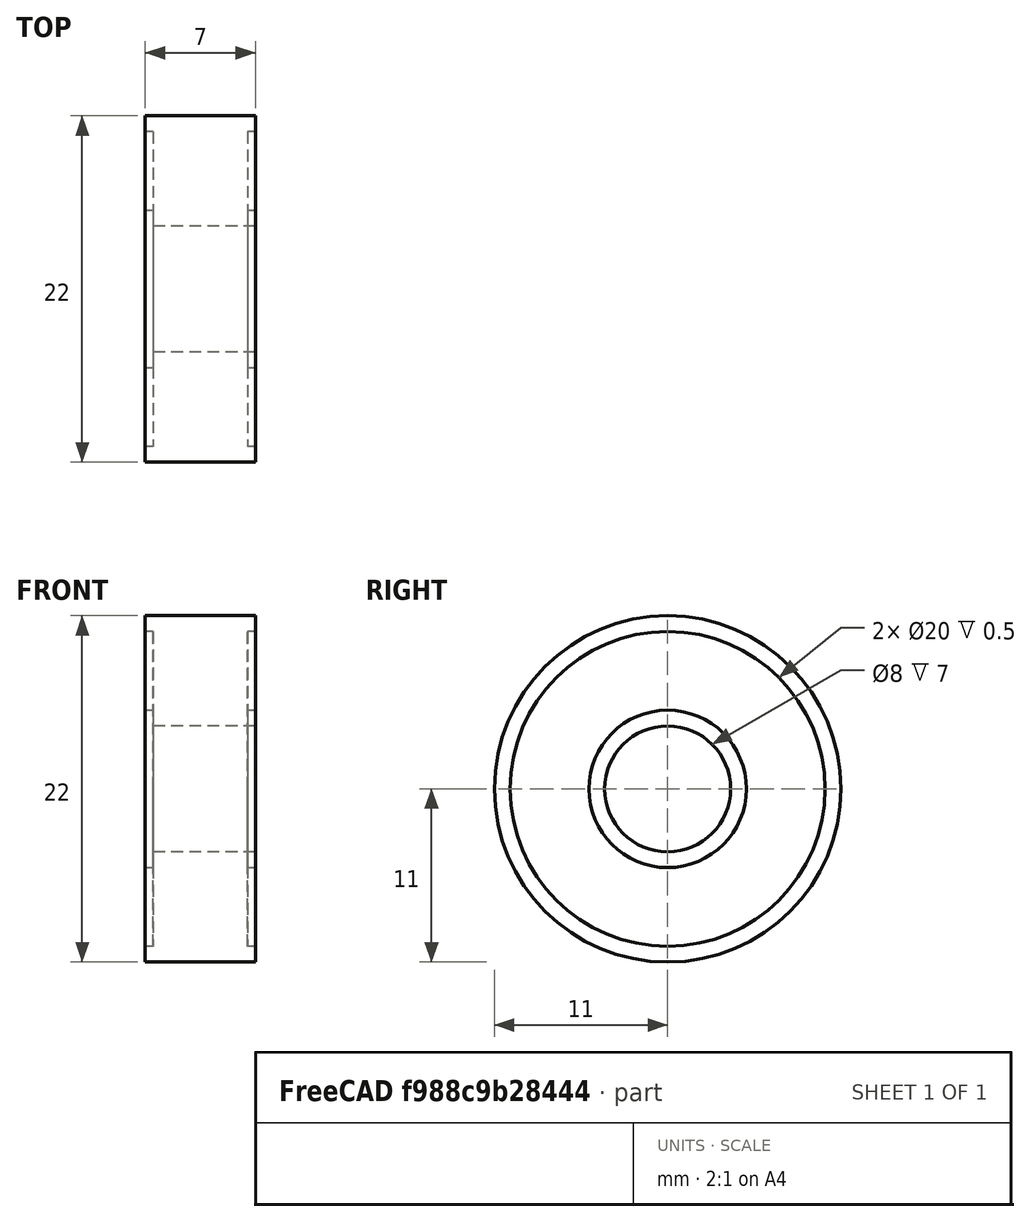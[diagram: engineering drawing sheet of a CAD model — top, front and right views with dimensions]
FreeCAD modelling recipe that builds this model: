
FCSTD DOCUMENT  (FreeCAD 0.16R6712 (Git))
Label: 608bearing
License: All rights reserved
LicenseURL: http://en.wikipedia.org/wiki/All_rights_reserved
objects: Sketcher::SketchObject×1, PartDesign::Revolution×1
note: 3 computed .brp shape members not serialized (recipe doc carries the construction recipe); baked Part::Feature solids carry a one-line shape summary decoded from their .brp

FEATURE [Sketcher::SketchObject] Sketch
  sketch-geometry (12):
    g0: LineSegment StartX=3.5 StartY=4 StartZ=0 EndX=-3.5 EndY=4 EndZ=0
    g1: LineSegment StartX=-3.5 StartY=4 StartZ=0 EndX=-3.5 EndY=5 EndZ=0
    g2: LineSegment StartX=-3.5 StartY=5 StartZ=0 EndX=-3 EndY=5 EndZ=0
    g3: LineSegment StartX=-3 StartY=5 StartZ=0 EndX=-3 EndY=10 EndZ=0
    g4: LineSegment StartX=-3 StartY=10 StartZ=0 EndX=-3.5 EndY=10 EndZ=0
    g5: LineSegment StartX=-3.5 StartY=10 StartZ=0 EndX=-3.5 EndY=11 EndZ=0
    g6: LineSegment StartX=-3.5 StartY=11 StartZ=0 EndX=3.5 EndY=11 EndZ=0
    g7: LineSegment StartX=3.5 StartY=11 StartZ=0 EndX=3.5 EndY=10 EndZ=0
    g8: LineSegment StartX=3.5 StartY=10 StartZ=0 EndX=3 EndY=10 EndZ=0
    g9: LineSegment StartX=3 StartY=10 StartZ=0 EndX=3 EndY=5 EndZ=0
    g10: LineSegment StartX=3 StartY=5 StartZ=0 EndX=3.5 EndY=5 EndZ=0
    g11: LineSegment StartX=3.5 StartY=5 StartZ=0 EndX=3.5 EndY=4 EndZ=0
  constraints (34):
    c: Coincident(g0,g1)
    c: Vertical(g1)
    c: Coincident(g1,g2)
    c: Coincident(g2,g3)
    c: Vertical(g3)
    c: Coincident(g3,g4)
    c: Coincident(g4,g5)
    c: Vertical(g5)
    c: Coincident(g5,g6)
    c: Horizontal(g6)
    c: Coincident(g6,g7)
    c: Vertical(g7)
    c: Coincident(g7,g8)
    c: Horizontal(g8)
    c: Coincident(g8,g9)
    c: Coincident(g9,g10)
    c: Coincident(g10,g11)
    c: Coincident(g11,g0)
    c: Vertical(g9)
    c: Horizontal(g10)
    c: Vertical(g11)
    c: Horizontal(g4)
    c: Horizontal(g2)
    c: DistanceY(g5,g5) = 1
    c: DistanceY(g1,g1) = 1
    c: Symmetric(g5,g6,g-2)
    c: Symmetric(g3,g8,g-2)
    c: Symmetric(g2,g9,g-2)
    c: Symmetric(g0,g0,g-2)
    c: DistanceX(g0,g0) = 7
    c: Equal(g6,g0)
    c: DistanceX(g3,g8) = 6
    c: DistanceY(g-1,g5) = 11
    c: DistanceY(g-1,g0) = 4
FEATURE [PartDesign::Revolution] Revolution
  Angle = 360
  Axis = (1,0,0)
  Base = (0,0,0)
  ReferenceAxis = -> Sketch [H_Axis]
  Sketch = -> Sketch
